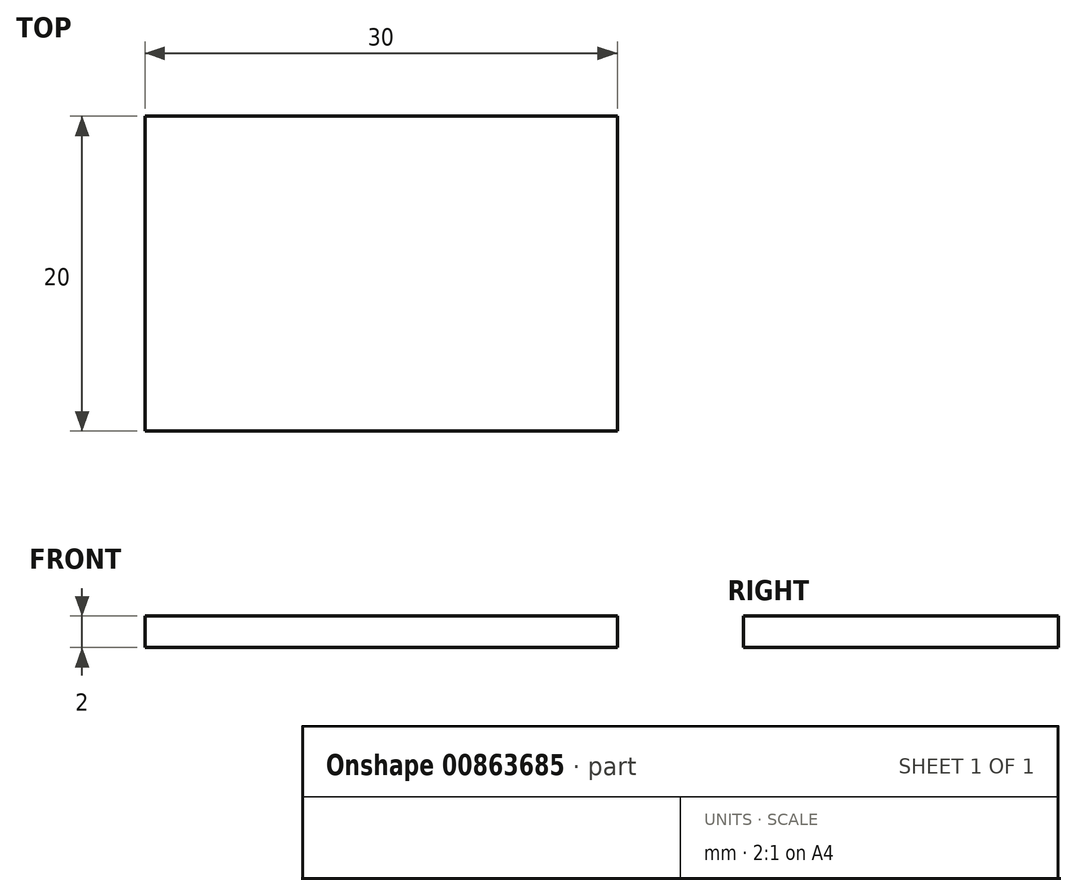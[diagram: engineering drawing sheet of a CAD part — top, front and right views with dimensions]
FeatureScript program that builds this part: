
annotation { "Feature Type Name" : "Feature", "Feature Type Description" : "" }
export const myFeature = defineFeature(function(context is Context, id is Id, definition is map)
    precondition{}
    {
        {
            var Q0;
            Q0=qCreatedBy(makeId("Top.planeOp"),FACE);
            var sketch = newSketch(context, id + "F0", { "sketchPlane" : qUnion([Q0])});
            skLineSegment(sketch, "E0.bottom", {"start": v(0, 0) * mm, "end": v(30, 0) * mm});
            skLineSegment(sketch, "E0.top", {"start": v(0, 20) * mm, "end": v(30, 20) * mm});
            skLineSegment(sketch, "E0.left", {"start": v(0, 0) * mm, "end": v(0, 20) * mm});
            skLineSegment(sketch, "E0.right", {"start": v(30, 0) * mm, "end": v(30, 20) * mm});
            skSolve(sketch);
        }
        {
            var Q0;
            Q0=makeQuery(id+"F0.imprint","IMPRINT",FACE,{"disambiguationData":[TD([[makeQuery(id+"F0.imprint","IMPRINT",EDGE,{"derivedFrom":sQuery(id+"F0.wireOp",EDGE,"E0.bottom")}),1.0]])]});
            extrude(context, id + "F1", {"entities" : qUnion([Q0]), "depth" : 2 * mm, "offsetDistance" : 25 * mm});
        }
    });
